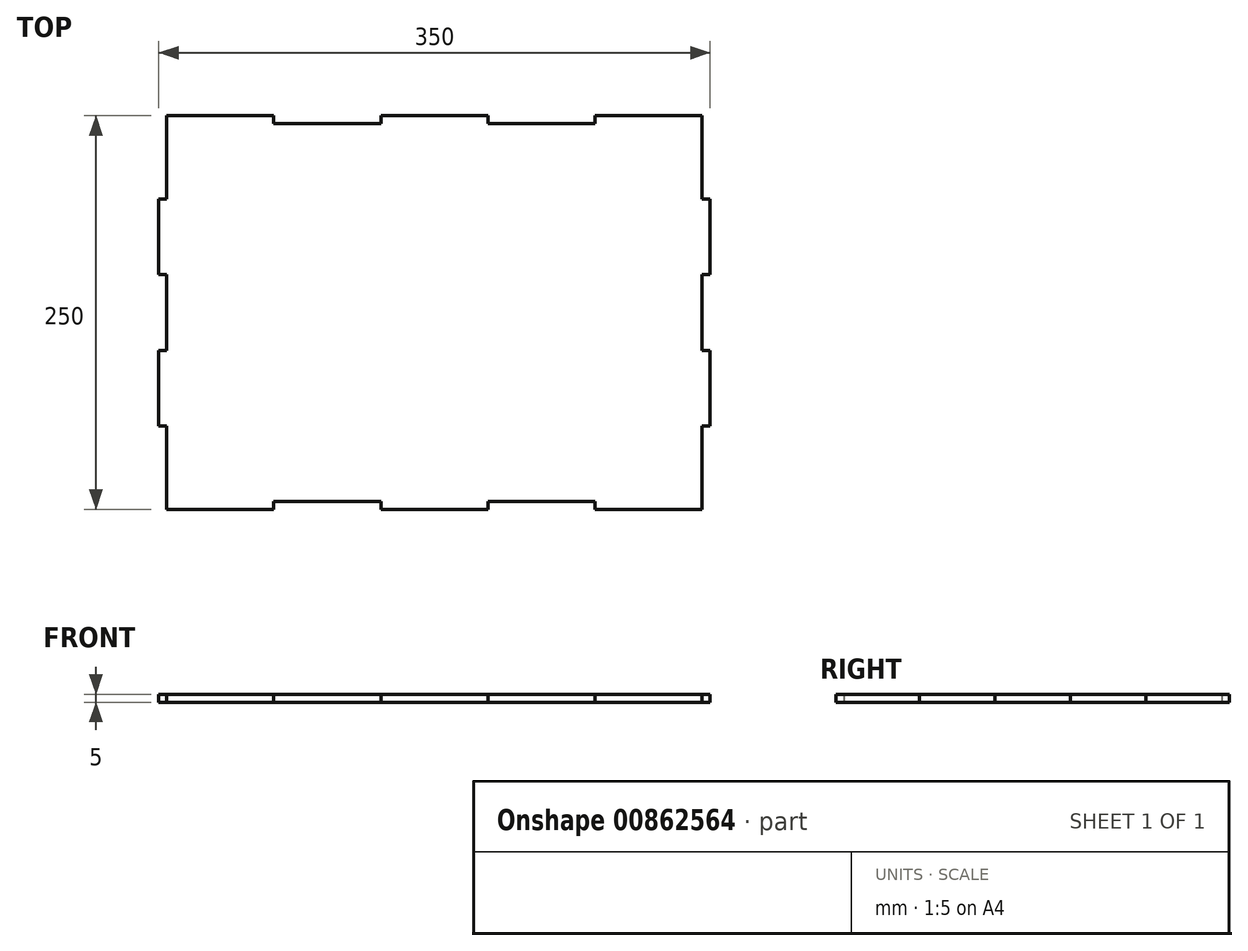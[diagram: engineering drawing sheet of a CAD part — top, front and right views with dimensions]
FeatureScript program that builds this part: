
annotation { "Feature Type Name" : "Feature", "Feature Type Description" : "" }
export const myFeature = defineFeature(function(context is Context, id is Id, definition is map)
    precondition{}
    {
        {
            var Q0;
            Q0=qCreatedBy(makeId("Top.planeOp"),FACE);
            var sketch = newSketch(context, id + "F0", { "sketchPlane" : qUnion([Q0])});
            skLineSegment(sketch, "E0.bottom", {"start": v(170, -120) * mm, "end": v(-170, -120) * mm});
            skLineSegment(sketch, "E0.top", {"start": v(170, 120) * mm, "end": v(-170, 120) * mm});
            skLineSegment(sketch, "E0.left", {"start": v(170, -120) * mm, "end": v(170, 120) * mm});
            skLineSegment(sketch, "E0.right", {"start": v(-170, -120) * mm, "end": v(-170, 120) * mm});
            skPoint(sketch, "E0.middle", {"position": v(0, 0) * mm});
            skLineSegment(sketch, "E1", {"start": v(-170, -120) * mm, "end": v(-170, -125) * mm});
            skLineSegment(sketch, "E2", {"start": v(-170, -125) * mm, "end": v(-102, -125) * mm});
            skLineSegment(sketch, "E3", {"start": v(-102, -125) * mm, "end": v(-102, -120) * mm});
            skLineSegment(sketch, "E4.1.0.0", {"start": v(34, -125) * mm, "end": v(34, -120) * mm});
            skLineSegment(sketch, "E4.1.0.1", {"start": v(-34, -120) * mm, "end": v(-34, -125) * mm});
            skLineSegment(sketch, "E4.1.0.2", {"start": v(-34, -125) * mm, "end": v(34, -125) * mm});
            skLineSegment(sketch, "E4.2.0.0", {"start": v(170, -125) * mm, "end": v(170, -120) * mm});
            skLineSegment(sketch, "E4.2.0.1", {"start": v(102, -120) * mm, "end": v(102, -125) * mm});
            skLineSegment(sketch, "E4.2.0.2", {"start": v(102, -125) * mm, "end": v(170, -125) * mm});
            skLineSegment(sketch, "E4.direction1", {"start": v(-170, -125) * mm, "end": v(-34, -125) * mm, "construction": true});
            skLineSegment(sketch, "E5.MirrorCS", {"start": v(-170, 120) * mm, "end": v(-170, 125) * mm});
            skLineSegment(sketch, "E6.MirrorCS", {"start": v(-34, 120) * mm, "end": v(-34, 125) * mm});
            skLineSegment(sketch, "E7.MirrorCS", {"start": v(170, 125) * mm, "end": v(170, 120) * mm});
            skLineSegment(sketch, "E8.MirrorCS", {"start": v(-102, 125) * mm, "end": v(-102, 120) * mm});
            skLineSegment(sketch, "E9.MirrorCS", {"start": v(102, 120) * mm, "end": v(102, 125) * mm});
            skLineSegment(sketch, "E10.MirrorCS", {"start": v(34, 125) * mm, "end": v(34, 120) * mm});
            skLineSegment(sketch, "E11.MirrorCS", {"start": v(-170, 125) * mm, "end": v(-102, 125) * mm});
            skLineSegment(sketch, "E12.MirrorCS", {"start": v(-170, 125) * mm, "end": v(-34, 125) * mm, "construction": true});
            skLineSegment(sketch, "E13.MirrorCS", {"start": v(-34, 125) * mm, "end": v(34, 125) * mm});
            skLineSegment(sketch, "E14.MirrorCS", {"start": v(102, 125) * mm, "end": v(170, 125) * mm});
            skLineSegment(sketch, "E15", {"start": v(-170, 72) * mm, "end": v(-175, 72) * mm});
            skLineSegment(sketch, "E16", {"start": v(-175, 72) * mm, "end": v(-175, 24) * mm});
            skLineSegment(sketch, "E17", {"start": v(-175, 24) * mm, "end": v(-170, 24) * mm});
            skLineSegment(sketch, "E18.0.1.0", {"start": v(-170, -24) * mm, "end": v(-175, -24) * mm});
            skLineSegment(sketch, "E18.0.1.1", {"start": v(-175, -24) * mm, "end": v(-175, -72) * mm});
            skLineSegment(sketch, "E18.0.1.2", {"start": v(-175, -72) * mm, "end": v(-170, -72) * mm});
            skLineSegment(sketch, "E18.direction2", {"start": v(-175, 72) * mm, "end": v(-175, -24) * mm, "construction": true});
            skLineSegment(sketch, "E19.MirrorCS", {"start": v(170, 72) * mm, "end": v(175, 72) * mm});
            skLineSegment(sketch, "E20.MirrorCS", {"start": v(170, -24) * mm, "end": v(175, -24) * mm});
            skLineSegment(sketch, "E21.MirrorCS", {"start": v(175, -72) * mm, "end": v(170, -72) * mm});
            skLineSegment(sketch, "E22.MirrorCS", {"start": v(175, 24) * mm, "end": v(170, 24) * mm});
            skLineSegment(sketch, "E23.MirrorCS", {"start": v(175, 72) * mm, "end": v(175, 24) * mm});
            skLineSegment(sketch, "E24.MirrorCS", {"start": v(175, 72) * mm, "end": v(175, -24) * mm, "construction": true});
            skLineSegment(sketch, "E25.MirrorCS", {"start": v(175, -24) * mm, "end": v(175, -72) * mm});
            skSolve(sketch);
        }
        {
            var Q0;
            Q0 = qSketchRegion(id + "F0", true);
            extrude(context, id + "F1", {"entities" : qUnion([Q0]), "depth" : 5 * mm, "offsetDistance" : 25 * mm});
        }
    });
